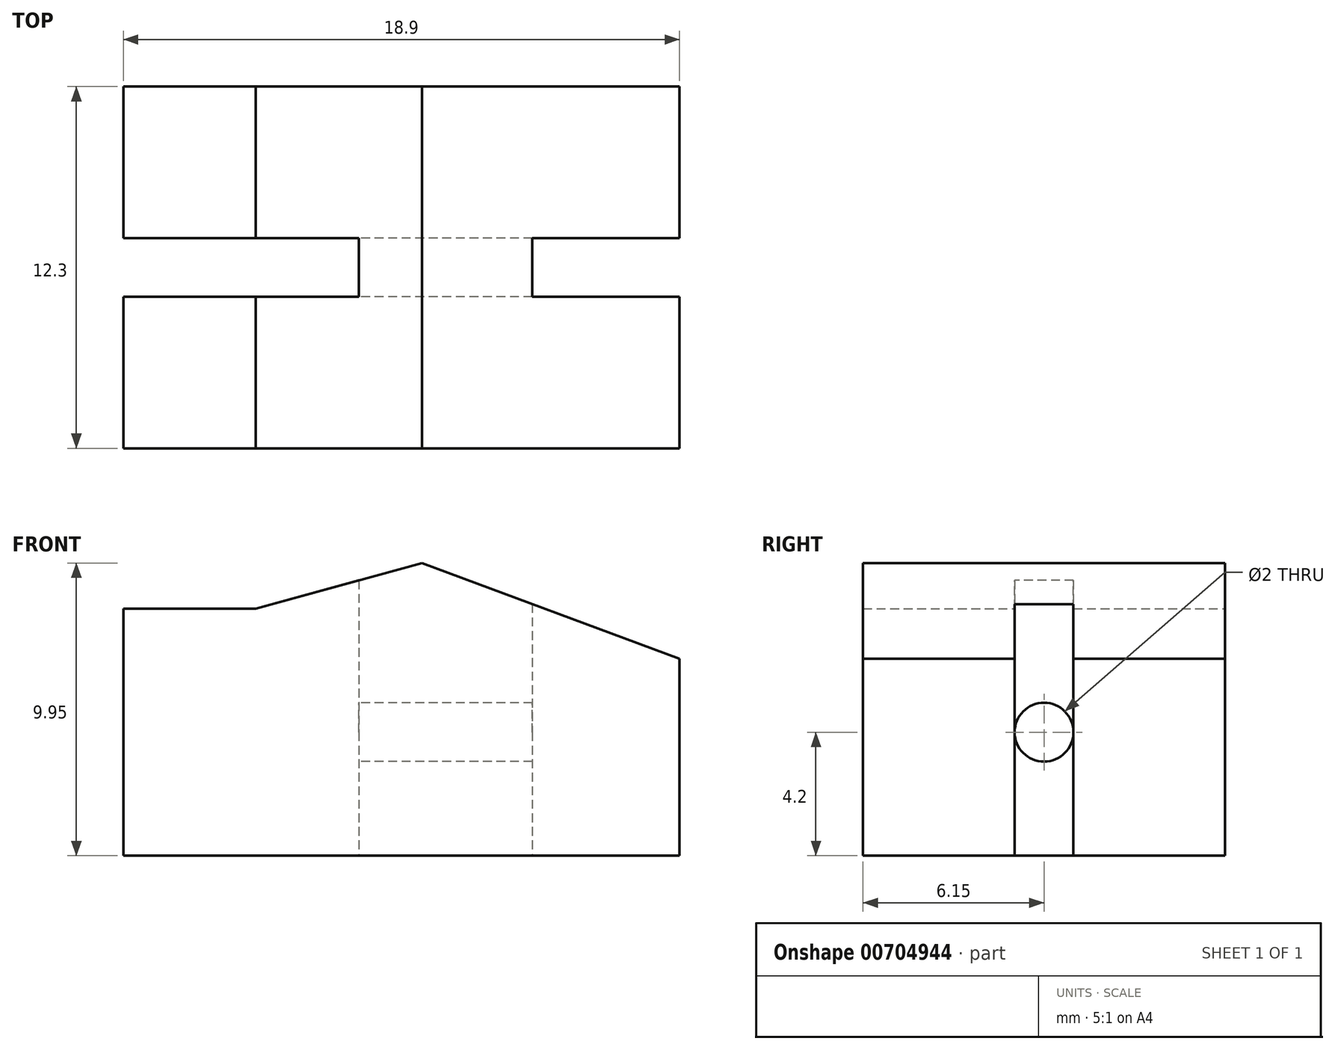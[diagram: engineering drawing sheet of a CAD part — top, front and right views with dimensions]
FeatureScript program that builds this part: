
annotation { "Feature Type Name" : "Feature", "Feature Type Description" : "" }
export const myFeature = defineFeature(function(context is Context, id is Id, definition is map)
    precondition{}
    {
        {
            var Q0;
            Q0=qCreatedBy(makeId("Front.planeOp"),FACE);
            var sketch = newSketch(context, id + "F0", { "sketchPlane" : qUnion([Q0])});
            skLineSegment(sketch, "E0", {"start": v(0, 8.4) * mm, "end": v(0, 0) * mm});
            skLineSegment(sketch, "E1", {"start": v(0, 0) * mm, "end": v(18.9, 0) * mm});
            skLineSegment(sketch, "E2", {"start": v(18.9, 0) * mm, "end": v(18.9, 6.7) * mm});
            skLineSegment(sketch, "E3", {"start": v(18.9, 6.7) * mm, "end": v(10.15, 9.95) * mm});
            skLineSegment(sketch, "E4", {"start": v(10.15, 9.95) * mm, "end": v(4.5, 8.4) * mm});
            skLineSegment(sketch, "E5", {"start": v(4.5, 8.4) * mm, "end": v(0, 8.4) * mm});
            skSolve(sketch);
        }
        {
            var Q0;
            Q0=makeQuery(id+"F0.imprint","IMPRINT",FACE,{"disambiguationData":[TD([[makeQuery(id+"F0.imprint","IMPRINT",EDGE,{"derivedFrom":sQuery(id+"F0.wireOp",EDGE,"E0")}),1.0]])]});
            extrude(context, id + "F1", {"entities" : qUnion([Q0]), "depth" : 12.3 * mm, "offsetDistance" : 25 * mm});
        }
        {
            var Q0;
            Q0=makeQuery(id+"F1.opExtrude","SWEPT_FACE",FACE,{"disambiguationData":[OSD([sQuery(id+"F0.wireOp",EDGE,"E1")])]});
            var sketch = newSketch(context, id + "F2", { "sketchPlane" : qUnion([Q0])});
            skPoint(sketch, "E6", {"position": v(0, 6.15) * mm});
            skPoint(sketch, "E7", {"position": v(18.9, 6.15) * mm});
            skLineSegment(sketch, "E8.bottom", {"start": v(0, 5.15) * mm, "end": v(8, 5.15) * mm});
            skLineSegment(sketch, "E8.top", {"start": v(0, 7.15) * mm, "end": v(8, 7.15) * mm});
            skLineSegment(sketch, "E8.left", {"start": v(0, 5.15) * mm, "end": v(0, 7.15) * mm});
            skLineSegment(sketch, "E8.right", {"start": v(8, 5.15) * mm, "end": v(8, 7.15) * mm});
            skPoint(sketch, "E8.middle", {"position": v(4, 6.15) * mm});
            skLineSegment(sketch, "E9.bottom", {"start": v(18.9, 7.15) * mm, "end": v(13.9, 7.15) * mm});
            skLineSegment(sketch, "E9.top", {"start": v(18.9, 5.15) * mm, "end": v(13.9, 5.15) * mm});
            skLineSegment(sketch, "E9.left", {"start": v(18.9, 7.15) * mm, "end": v(18.9, 5.15) * mm});
            skLineSegment(sketch, "E9.right", {"start": v(13.9, 7.15) * mm, "end": v(13.9, 5.15) * mm});
            skPoint(sketch, "E9.middle", {"position": v(16.4, 6.15) * mm});
            skSolve(sketch);
        }
        {
            var Q0;
            Q0=makeQuery(id+"F2.imprint","IMPRINT",FACE,{"disambiguationData":[TD([[makeQuery(id+"F2.imprint","IMPRINT",EDGE,{"derivedFrom":sQuery(id+"F2.wireOp",EDGE,"E8.bottom")}),1.0]])]});
            var Q1;
            Q1=makeQuery(id+"F2.imprint","IMPRINT",FACE,{"disambiguationData":[TD([[makeQuery(id+"F2.imprint","IMPRINT",EDGE,{"derivedFrom":sQuery(id+"F2.wireOp",EDGE,"E9.bottom")}),1.0]])]});
            extrude(context, id + "F3", {"entities" : qUnion([Q0, Q1]), "operationType" : NewBodyOperationType.REMOVE, "endBound" : BoundingType.THROUGH_ALL, "oppositeDirection" : true, "depth" : 25 * mm, "offsetDistance" : 25 * mm});
        }
        {
            var Q0;
            Q0=makeQuery(id+"F3.boolean.opBoolean","COPY",FACE,{"derivedFrom":makeQuery(id+"F3.opExtrude","SWEPT_FACE",FACE,{"disambiguationData":[OSD([sQuery(id+"F2.wireOp",EDGE,"E8.right")])]})});
            var sketch = newSketch(context, id + "F4", { "sketchPlane" : qUnion([Q0])});
            skLineSegment(sketch, "E10", {"start": v(12.3, 8.4) * mm, "end": v(0, 8.4) * mm, "construction": true});
            skLineSegment(sketch, "E11", {"start": v(12.3, 8.4) * mm, "end": v(12.3, 0) * mm, "construction": true});
            skLineSegment(sketch, "E12", {"start": v(12.3, 0) * mm, "end": v(0, 0) * mm, "construction": true});
            skLineSegment(sketch, "E13", {"start": v(0, 0) * mm, "end": v(0, 8.4) * mm, "construction": true});
            skPoint(sketch, "E14", {"position": v(6.15, 0) * mm});
            skPoint(sketch, "E15", {"position": v(0, 4.2) * mm});
            skCircle(sketch, "E16", {"center": v(6.15, 4.2) * mm, "radius": 1 * mm});
            skSolve(sketch);
        }
        {
            var Q0;
            {var subQ0=sQuery(id+"F4.wireOp",EDGE,"E16");var subQ1=sQuery(id+"F2.wireOp",EDGE,"E8.right");var subQ2=makeQuery(id+"F4.imprint","INTERSECT",VERTEX,{"derivedFrom":[makeQuery(id+"F3.boolean.opBoolean","COPY",EDGE,{"derivedFrom":makeQuery(id+"F3.opExtrude","SWEPT_EDGE",EDGE,{"disambiguationData":[OSD([sQuery(id+"F2.wireOp",EDGE,"E8.bottom"),subQ1])]})}),subQ0]});Q0=makeQuery(id+"F4.imprint","IMPRINT",FACE,{"disambiguationData":[TD([[makeQuery(id+"F4.imprint","IMPRINT",EDGE,{"disambiguationData":[TD([[subQ2,1.0]])],"derivedFrom":subQ0}),1.0]])]});}
            extrude(context, id + "F5", {"entities" : qUnion([Q0]), "operationType" : NewBodyOperationType.REMOVE, "endBound" : BoundingType.THROUGH_ALL, "oppositeDirection" : true, "depth" : 25 * mm, "offsetDistance" : 25 * mm});
        }
    });
